# Revit family: STH6338_24
name_source: partatom
category: Luminárias
units: mm (PartAtom-declared; Revit-internal decimal feet)

## family parameters
Com base no plano de trabalho = Não
Compartilhado = Não
Corte com vazios quando carregada = Não
Cota do conector redondo = Utilizar diâmetro
Fonte luminosa = Sim
Manter orientação da anotação = Não
Ponto de cálculo do ambiente = Não
Sempre na vertical = Sim
Tipo de parte = Normal

## types (1)
- STH6338/24 - BIVOLT - LUZ ÂMBAR - 200lm - 300°
    Altura = 0.14 m
    Arquivo de rede fotométrica = STELLA - STH6338-24 - ST64 FILAMENTO VINTAGE.ies
    Cromado = Cromado
    Dimerização = Não dimerizável
    Diâmetro = 0.06 m
    Elevação padrão = 0 m
    Emissivo = Luz Âmbar
    Fabricante = Stella
    Filtro de cor = 16777215
    Glass = Vidro
    Grau de proteção (IP) = IP20
    IRC (Índice de reprodução de cores) = >80
    Modelo = ST64 Vintage Filamento
    Potência = 2 W
    Tensão Elétrica = 100V-240V
    Troca de temperatura da cor de lâmpada com esmaecimento = <Nenhum>
    URL = https://stella.com.br
    Ângulo de Abertura = 300°
    Ângulo de inclinação = 90.00°
